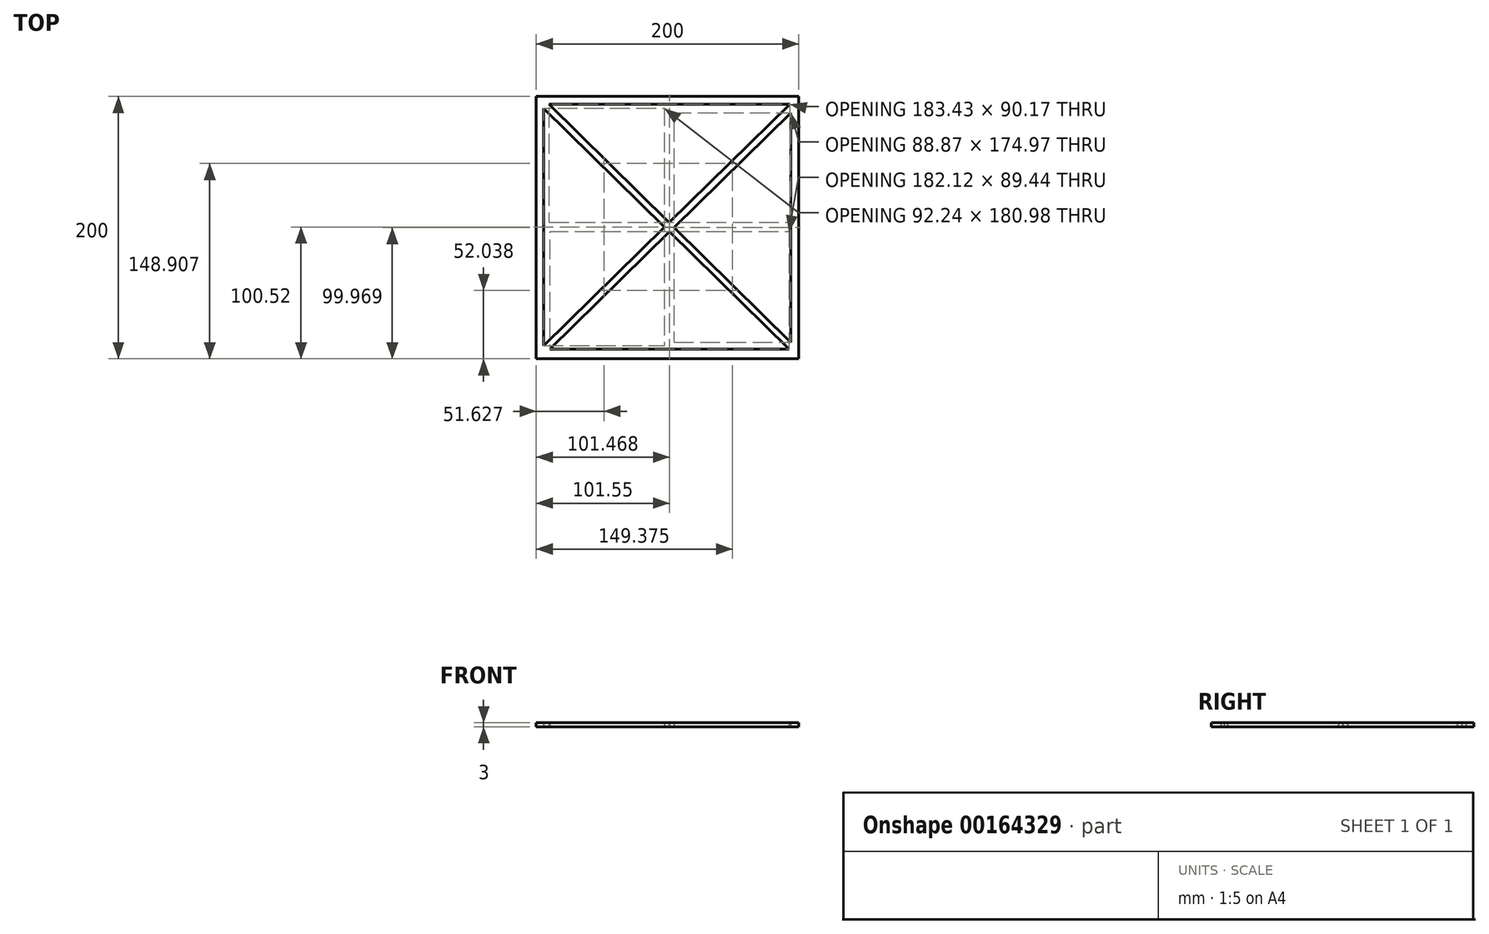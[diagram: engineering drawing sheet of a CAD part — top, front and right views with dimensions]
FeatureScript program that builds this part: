
annotation { "Feature Type Name" : "Feature", "Feature Type Description" : "" }
export const myFeature = defineFeature(function(context is Context, id is Id, definition is map)
    precondition{}
    {
        {
            var Q0;
            Q0=qCreatedBy(makeId("Top.planeOp"),FACE);
            var sketch = newSketch(context, id + "F0", { "sketchPlane" : qUnion([Q0])});
            skLineSegment(sketch, "E0.bottom", {"start": v(-100.15, 112.6) * mm, "end": v(99.85, 112.6) * mm});
            skLineSegment(sketch, "E0.top", {"start": v(-100.15, -87.4) * mm, "end": v(99.85, -87.4) * mm});
            skLineSegment(sketch, "E0.left", {"start": v(-100.15, 112.6) * mm, "end": v(-100.15, -87.4) * mm});
            skLineSegment(sketch, "E0.right", {"start": v(99.85, 112.6) * mm, "end": v(99.85, -87.4) * mm});
            skLineSegment(sketch, "E1.bottom", {"start": v(-90.31, 106.6) * mm, "end": v(93.11, 106.6) * mm});
            skLineSegment(sketch, "E1.top", {"start": v(-89.74, -80.08) * mm, "end": v(92.38, -80.08) * mm});
            skLineSegment(sketch, "E1.left", {"start": v(-94.64, 103.61) * mm, "end": v(-94.64, -77.37) * mm});
            skLineSegment(sketch, "E1.right", {"start": v(93.66, 100.06) * mm, "end": v(93.66, -74.92) * mm});
            skLineSegment(sketch, "E2", {"start": v(-90.31, 106.6) * mm, "end": v(1.08, 16.42) * mm});
            skLineSegment(sketch, "E3", {"start": v(-94.64, 103.61) * mm, "end": v(-2.4, 13) * mm});
            skLineSegment(sketch, "E4", {"start": v(93.11, 106.6) * mm, "end": v(1.08, 16.42) * mm});
            skLineSegment(sketch, "E5", {"start": v(93.66, 100.06) * mm, "end": v(4.79, 12.77) * mm});
            skLineSegment(sketch, "E6.trimOffspring", {"start": v(-2.4, 13) * mm, "end": v(-94.64, -77.37) * mm});
            skLineSegment(sketch, "E7.trimOffspring", {"start": v(4.79, 12.77) * mm, "end": v(93.66, -74.92) * mm});
            skLineSegment(sketch, "E8.trimOffspring", {"start": v(1.32, 9.36) * mm, "end": v(-89.74, -80.08) * mm});
            skLineSegment(sketch, "E9.trimOffspring", {"start": v(1.32, 9.36) * mm, "end": v(92.38, -80.08) * mm});
            skSolve(sketch);
        }
        {
            var Q0;
            Q0 = qSketchRegion(id + "F0", true);
            extrude(context, id + "F1", {"entities" : qUnion([Q0]), "depth" : 3 * mm});
        }
    });
